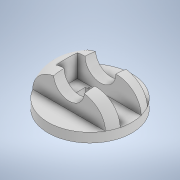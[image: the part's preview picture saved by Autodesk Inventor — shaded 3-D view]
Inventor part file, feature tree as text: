
AUTODESK INVENTOR PART (.ipt)
format: ipt  version: 2022 (Build 260153000, 153)  size: 220,160 bytes
history: native  units: mm
features: extrude x8, sketch x8, fillet x1
ambient origin geometry x8: Origin, YZ Plane, XZ Plane, XY Plane, X Axis, Y Axis, Z Axis, Center Point
bodies: Solid1 (feature_tree)
feature tree (17):
  extrude  "Extrusion1"  Depth=100.0mm TaperAngle=0.0deg
  extrude  "Extrusion2"  Depth=45.0mm
  extrude  "Extrusion3"  Depth=90.0mm
  extrude  "Extrusion4"  Depth=30.0mm
  extrude  "Extrusion5"  Depth=50.0mm TaperAngle=0.0deg
  fillet  "Fillet1"  Radius=20.0mm
  extrude  "Extrusion6"  Depth=15.0mm
  extrude  "Extrusion7"  Depth=10.0mm
  extrude  "Extrusion8"  Depth=5.0mm TaperAngle=0.0deg
  sketch  "Sketch1"  dims[d0=180.0mm d1=100.0mm d2=0.0mm]
  sketch  "Sketch2"  dims[d3=45.0mm d4=45.0mm]
  sketch  "Sketch3"  dims[d5=90.0mm d6=90.0mm]
  sketch  "Sketch4"  dims[d7=60.0mm d8=0.0mm d9=30.0mm]
  sketch  "Sketch5"  dims[d10=108.75mm d11=0.0mm d16=50.0mm d17=0.0mm d18=20.0mm d19=0.0mm]
  sketch  "Sketch6"  dims[d20=50.0mm d21=15.0mm]
  sketch  "Sketch7"  dims[d23=10.0mm d24=10.0mm]
  sketch  "Sketch10"  dims[d25=20.0mm d26=0.0mm d27=137.75mm d28=0.0mm d34=3.0mm d37=3.0mm d40=3.0mm d43=3.0mm d44=5.0mm d45=0.0mm]
